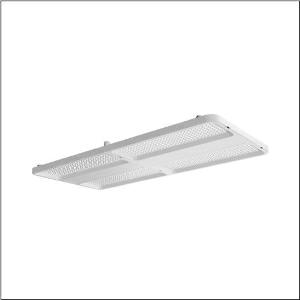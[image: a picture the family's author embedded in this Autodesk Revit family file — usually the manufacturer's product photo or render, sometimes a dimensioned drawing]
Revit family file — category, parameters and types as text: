
# Revit family: highbay_21_maxi_52hn11db5lda
name_source: partatom
category: Lighting Fixtures
units: mm (PartAtom-declared; Revit-internal decimal feet)

## family parameters
Cut with Voids When Loaded = No
Host = Face
Light Source = No
Part Type = Normal
Room Calculation Point = No
Round Connector Dimension = Use Diameter
Shared = No

## types (1)
- --- (1 x LED, 4120 lm, 22.6 W, 5000K)
    Apparent Load = 23 VA
    CIE Flux Codes = 89 97 99 100 100
    Color Rendering = 80
    Color Temperature = 5000K
    Default Elevation = 1800 mm
    Description = high bay luminaire Highbay 21 maxi; direct symmetric narrow distribution, light control with lens of PMMA; UGR ≤ 19 (X = 4H | Y = 8H | S = 0.25H | reflection values 70/50/20); luminous flux: 27.240lm; light colour: 850, colour temperature: 5000K, MacAdam ≤ 3 SDCM (initial), colour rendering: CRI > 80; luminous efficacy: 189,2lm/W; rated service life: 75.000h (L80) at AT= ta max; control: DALI 2; luminaire connection: terminal, 5-pole, max. 2.5mm² (cable entry for one cable, Ø 8.5..16mm); mains connection: 230..240V, AC/DC 0/50..60Hz; connected load: 144W; protection rating (complete): IP66; insulation class (complete): insulation class I (protective earthing); protection symbol: D; impact resistance: IK08; certification: CE, ENEC, VDE, UKCA; luminaire for central battery installations according to EN 60598-2-22, internal wiring halogen-free; luminaire LABS conformity tested according to VDMA 24364:2018-05; Suitable for use in the food industry according to the specifications of IFS-Food, HACCP and/or BRC; housing frame of high-performance plastic PA6, matt traffic white (RAL 9016); cover of PMMA; dimension (LxWxH): 946 x 442 x 72mm; permissible operating ambient temperature: -40..+65°C (reducing of maximum allowable ambient temperature of 5°C with ceiling mounting); packaging unit: 1 piece; (delivery without accessories; please order mounting accessories separately)
    Height = 72 mm  [stored 0.23622 ft]
    Lamp = 1 x LED
    Lamp Light Flux = 4120 lm
    Lamp Power = 22.6 W
    Lamp count = 1
    Length = 946 mm
    Luminous efficacy = 182 lm/W
    Manufacturer = Siteco
    ModVariant = No
    Model = 52HN11DB5LDA
    Mounting Place = Ceiling
    Mounting Type = Pendant
    Number of Poles = 1
    OnlyDefault = Yes
    Power Factor = 1
    Product Name = Highbay 21 maxi
    Product group = high bay luminaire
    ProductGroupID = 902
    Protection Class = Protection class I
    Protection Degree = IP 66
    RLX_Detail_Level = 1
    RLX_Emergency_Light_Flux = 0 lm
    RLX_Emergency_Type = 0
    RLX_Emergency_Type_DB = No
    RlxData = <blob elided: 128733 chars, md5=54ce7a73>
    Socket = socket
    Standby Power = 0 W
    System Light Flux = 4120 lm
    System Power = 23 W
    Type Comments = : DC mode (central or group accumulator) initial emergency light level
    Type Image = l_1363244.jpg
    URL = http://relux.com
    VarID = @adj_003301
    Voltage = 0 V
    Weight = 0.00 kg
    Width = 442 mm

note: [stored X ft] marks values corroborated as IEEE doubles in the binary element streams (Revit-internal decimal feet)

## geometry (parser evidence)
native form markers: Blend x4, Sweep x9
no freeform markers — native parametric forms only
